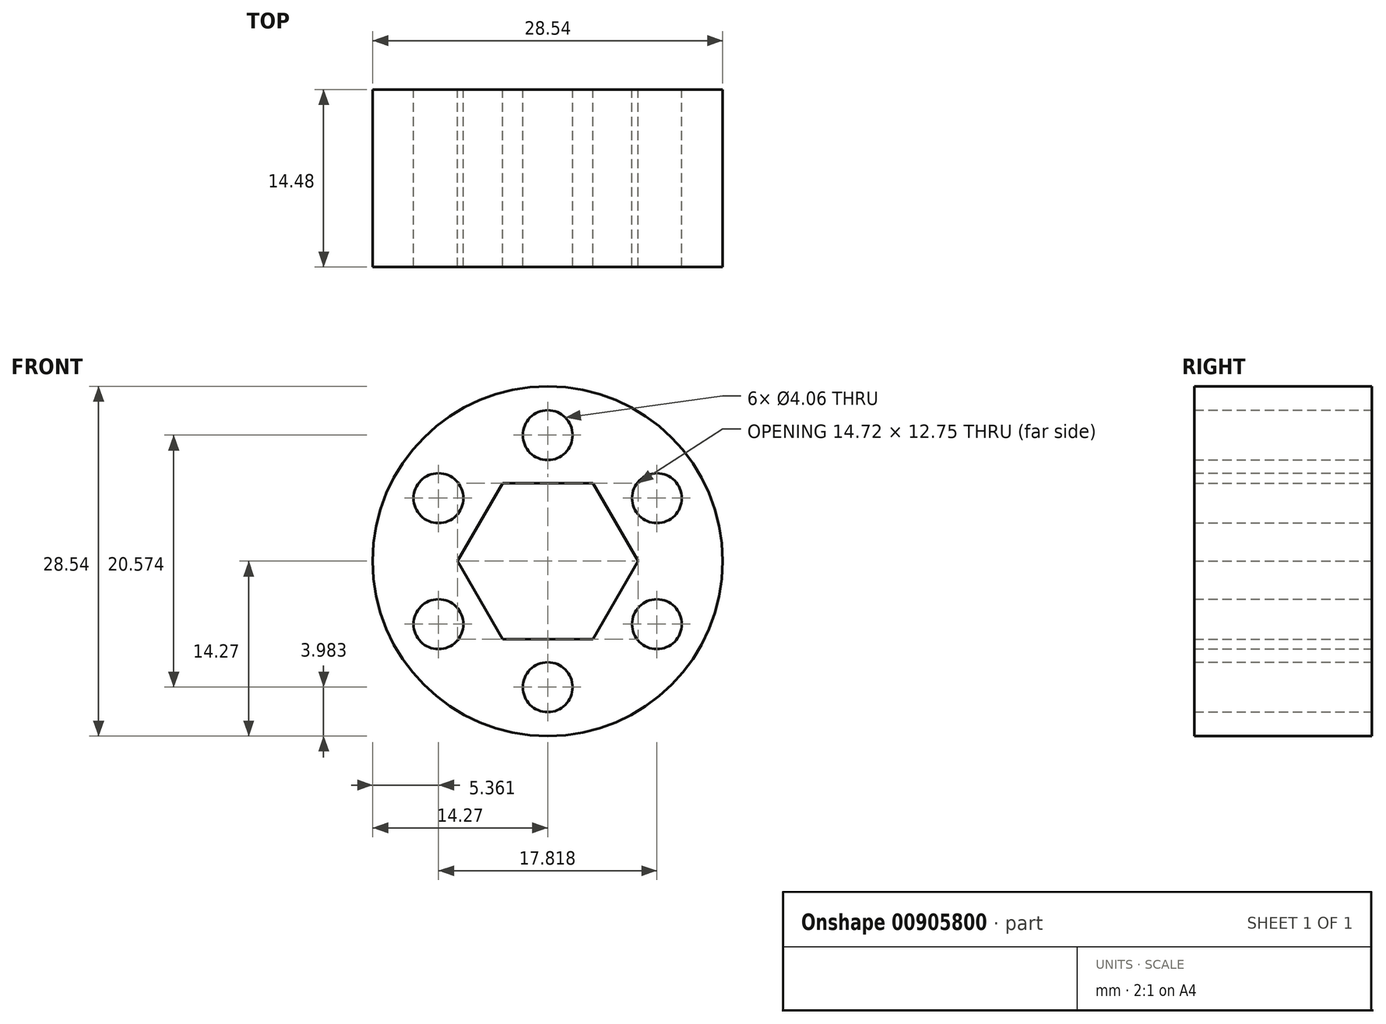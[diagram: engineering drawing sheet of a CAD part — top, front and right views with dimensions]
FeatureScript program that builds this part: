
annotation { "Feature Type Name" : "Feature", "Feature Type Description" : "" }
export const myFeature = defineFeature(function(context is Context, id is Id, definition is map)
    precondition{}
    {
        {
            var Q0;
            Q0=qCreatedBy(makeId("Front.planeOp"),FACE);
            var sketch = newSketch(context, id + "F0", { "sketchPlane" : qUnion([Q0])});
            skCircle(sketch, "E0", {"center": v(0, 0) * mm, "radius": 14.27 * mm});
            skCircle(sketch, "E1.cCircle", {"center": v(0, 0) * mm, "radius": 6.38 * mm, "construction": true});
            skLineSegment(sketch, "E1.0", {"start": v(7.36, 0) * mm, "end": v(3.68, -6.38) * mm});
            skLineSegment(sketch, "E1.1", {"start": v(3.68, -6.38) * mm, "end": v(-3.68, -6.38) * mm});
            skLineSegment(sketch, "E1.2", {"start": v(-3.68, -6.38) * mm, "end": v(-7.36, 0) * mm});
            skLineSegment(sketch, "E1.3", {"start": v(-7.36, 0) * mm, "end": v(-3.68, 6.38) * mm});
            skLineSegment(sketch, "E1.4", {"start": v(-3.68, 6.38) * mm, "end": v(3.68, 6.38) * mm});
            skLineSegment(sketch, "E1.5", {"start": v(3.68, 6.38) * mm, "end": v(7.36, 0) * mm});
            skPoint(sketch, "E1.0.midPoint", {"position": v(5.52, -3.19) * mm});
            skCircle(sketch, "E2", {"center": v(0, 10.29) * mm, "radius": 2.03 * mm});
            skCircle(sketch, "E3.1.0", {"center": v(-8.9, 5.14) * mm, "radius": 2.03 * mm});
            skCircle(sketch, "E3.2.0", {"center": v(-8.9, -5.14) * mm, "radius": 2.03 * mm});
            skCircle(sketch, "E3.3.0", {"center": v(0, -10.29) * mm, "radius": 2.03 * mm});
            skCircle(sketch, "E3.4.0", {"center": v(8.9, -5.14) * mm, "radius": 2.03 * mm});
            skCircle(sketch, "E3.5.0", {"center": v(8.9, 5.14) * mm, "radius": 2.03 * mm});
            skSolve(sketch);
        }
        {
            var Q0;
            Q0=qSketchRegion(id+"F0",true);
            extrude(context, id + "F1", {"entities" : qUnion([Q0]), "depth" : 14.48 * mm});
        }
    });
